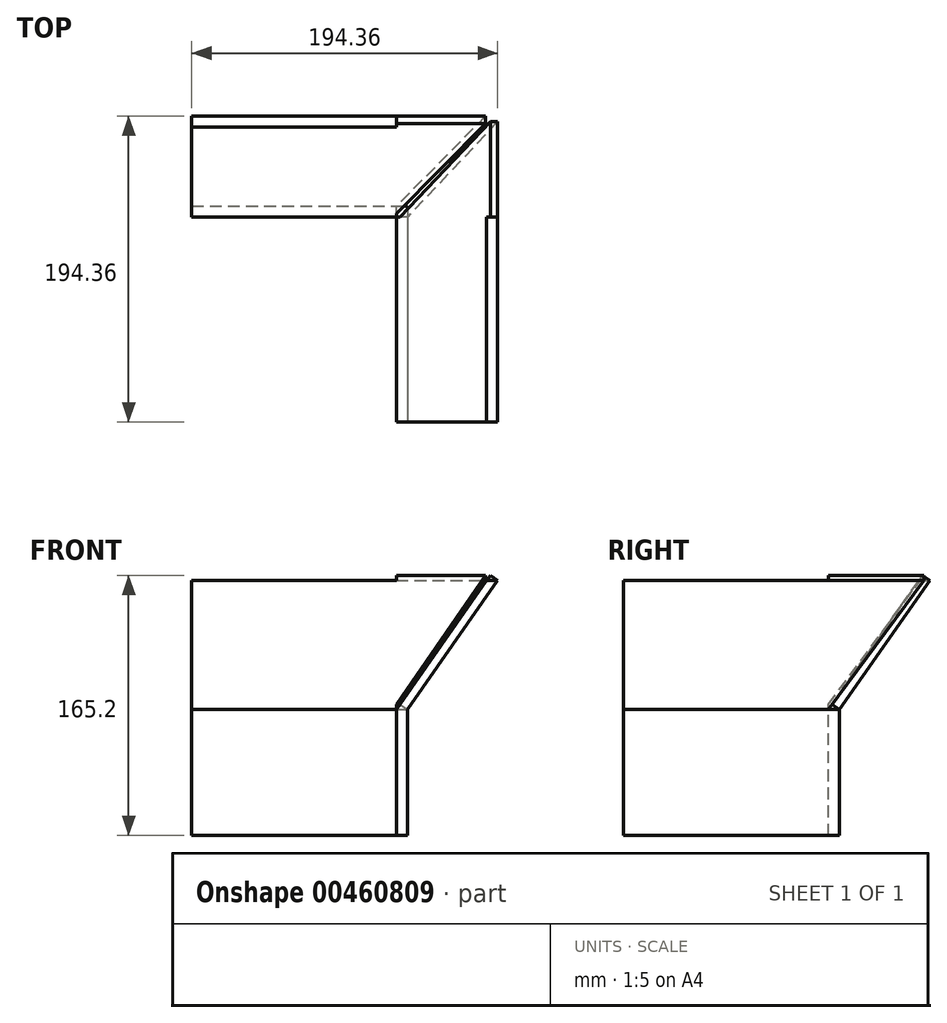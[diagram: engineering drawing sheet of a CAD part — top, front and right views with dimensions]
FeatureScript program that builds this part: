
annotation { "Feature Type Name" : "Feature", "Feature Type Description" : "" }
export const myFeature = defineFeature(function(context is Context, id is Id, definition is map)
    precondition{}
    {
        {
            var Q0;
            Q0=qCreatedBy(makeId("Top.planeOp"),FACE);
            var sketch = newSketch(context, id + "F0", { "sketchPlane" : qUnion([Q0])});
            skLineSegment(sketch, "E0", {"start": v(-130, 0) * mm, "end": v(0, 0) * mm});
            skLineSegment(sketch, "E1", {"start": v(0, 0) * mm, "end": v(0, -130) * mm});
            skLineSegment(sketch, "E2", {"start": v(-130, 0) * mm, "end": v(-130, 7) * mm});
            skLineSegment(sketch, "E3", {"start": v(-130, 7) * mm, "end": v(7, 7) * mm});
            skLineSegment(sketch, "E4", {"start": v(7, 7) * mm, "end": v(7, -130) * mm});
            skLineSegment(sketch, "E5", {"start": v(7, -130) * mm, "end": v(0, -130) * mm});
            skSolve(sketch);
        }
        {
            var Q0;
            Q0 = qSketchRegion(id + "F0", true);
            extrude(context, id + "F1", {"entities" : qUnion([Q0]), "oppositeDirection" : true, "depth" : 80 * mm});
        }
        {
            var Q0;
            Q0=makeQuery(id+"F1.opExtrude","SWEPT_FACE",FACE,{"disambiguationData":[OSD([sQuery(id+"F0.wireOp",EDGE,"E5")])]});
            var sketch = newSketch(context, id + "F2", { "sketchPlane" : qUnion([Q0])});
            skLineSegment(sketch, "E6", {"start": v(0, 0) * mm, "end": v(57.36, 81.92) * mm});
            skLineSegment(sketch, "E7", {"start": v(57.36, 81.92) * mm, "end": v(64.36, 81.92) * mm});
            skLineSegment(sketch, "E8", {"start": v(64.36, 81.92) * mm, "end": v(7, 0) * mm});
            skSolve(sketch);
        }
        {
            var Q0;
            Q0=makeQuery(id+"F2.imprint","IMPRINT",FACE,{"disambiguationData":[TD([[makeQuery(id+"F2.imprint","IMPRINT",EDGE,{"derivedFrom":sQuery(id+"F2.wireOp",EDGE,"E6")}),-1.0]])]});
            extrude(context, id + "F3", {"entities" : qUnion([Q0]), "operationType" : NewBodyOperationType.ADD, "oppositeDirection" : true, "depth" : 130 * mm});
        }
        {
            var Q0;
            Q0=makeQuery(id+"F1.opExtrude","SWEPT_FACE",FACE,{"disambiguationData":[OSD([sQuery(id+"F0.wireOp",EDGE,"E2")])]});
            var sketch = newSketch(context, id + "F4", { "sketchPlane" : qUnion([Q0])});
            skLineSegment(sketch, "E9", {"start": v(0, 0) * mm, "end": v(-57.36, 81.92) * mm});
            skLineSegment(sketch, "E10", {"start": v(-57.36, 81.92) * mm, "end": v(-64.36, 81.92) * mm});
            skLineSegment(sketch, "E11", {"start": v(-64.36, 81.92) * mm, "end": v(-7, 0) * mm});
            skSolve(sketch);
        }
        {
            var Q0;
            Q0=makeQuery(id+"F4.imprint","IMPRINT",FACE,{"disambiguationData":[TD([[makeQuery(id+"F4.imprint","IMPRINT",EDGE,{"derivedFrom":sQuery(id+"F4.wireOp",EDGE,"E9")}),1.0]])]});
            extrude(context, id + "F5", {"entities" : qUnion([Q0]), "operationType" : NewBodyOperationType.ADD, "oppositeDirection" : true, "depth" : 130 * mm});
        }
        {
            var Q0;
            Q0=makeQuery(id+"F3.opExtrude","SWEPT_FACE",FACE,{"disambiguationData":[OSD([sQuery(id+"F2.wireOp",EDGE,"E8")])]});
            var sketch = newSketch(context, id + "F6", { "sketchPlane" : qUnion([Q0])});
            skLineSegment(sketch, "E12", {"start": v(0, 104.02) * mm, "end": v(60.78, 104.02) * mm});
            skLineSegment(sketch, "E13", {"start": v(60.78, 104.02) * mm, "end": v(0, 4.02) * mm});
            skSolve(sketch);
        }
        {
            var Q0;
            Q0=makeQuery(id+"F6.imprint","IMPRINT",FACE,{"disambiguationData":[TD([[makeQuery(id+"F6.imprint","IMPRINT",EDGE,{"derivedFrom":sQuery(id+"F6.wireOp",EDGE,"E12")}),-1.0]])]});
            var Q1;
            Q1=makeQuery(id+"F3.opExtrude","SWEPT_FACE",FACE,{"disambiguationData":[OSD([sQuery(id+"F2.wireOp",EDGE,"E6")])]});
            extrude(context, id + "F7", {"entities" : qUnion([Q0]), "operationType" : NewBodyOperationType.ADD, "endBound" : BoundingType.UP_TO_SURFACE, "oppositeDirection" : true, "endBoundEntityFace" : qUnion([Q1]), "depth" : 5 * mm});
        }
        {
            var Q0;
            Q0=makeQuery(id+"F5.opExtrude","SWEPT_FACE",FACE,{"disambiguationData":[OSD([sQuery(id+"F4.wireOp",EDGE,"E11")])]});
            var sketch = newSketch(context, id + "F8", { "sketchPlane" : qUnion([Q0])});
            skLineSegment(sketch, "E14", {"start": v(0, 104.02) * mm, "end": v(-56.74, 104.02) * mm});
            skLineSegment(sketch, "E15", {"start": v(-56.74, 104.02) * mm, "end": v(0, 4.02) * mm});
            skSolve(sketch);
        }
        {
            var Q0;
            Q0=makeQuery(id+"F8.imprint","IMPRINT",FACE,{"disambiguationData":[TD([[makeQuery(id+"F8.imprint","IMPRINT",EDGE,{"derivedFrom":sQuery(id+"F8.wireOp",EDGE,"E14")}),1.0]])]});
            var Q1;
            Q1=makeQuery(id+"F5.opExtrude","SWEPT_FACE",FACE,{"disambiguationData":[OSD([sQuery(id+"F4.wireOp",EDGE,"E9")])]});
            extrude(context, id + "F9", {"entities" : qUnion([Q0]), "operationType" : NewBodyOperationType.ADD, "endBound" : BoundingType.UP_TO_SURFACE, "oppositeDirection" : true, "endBoundEntityFace" : qUnion([Q1]), "depth" : 25 * mm});
        }
    });
